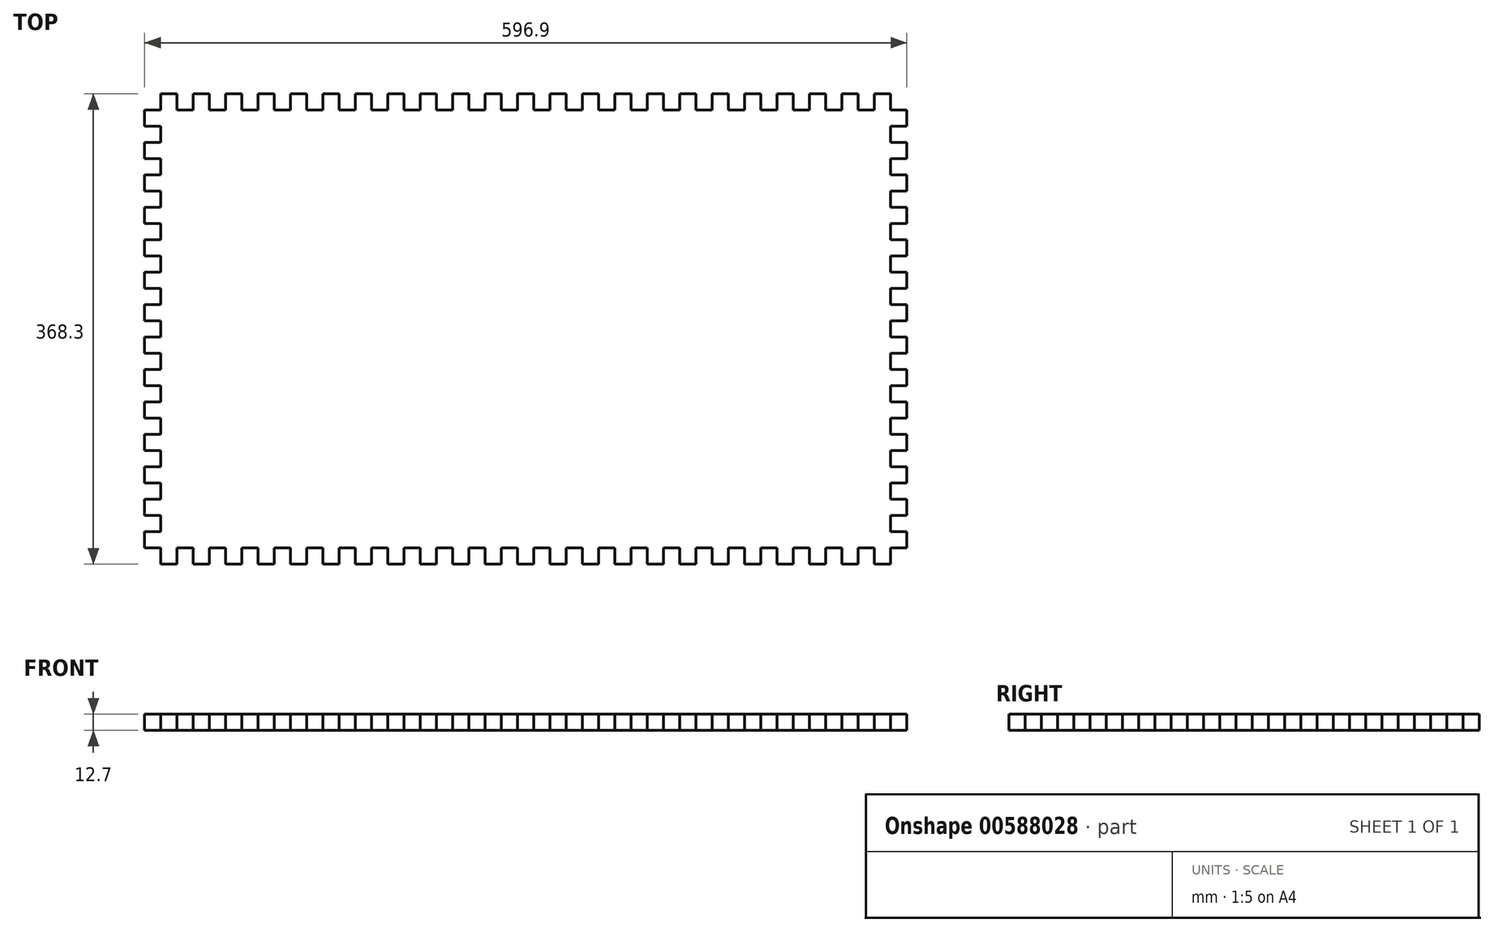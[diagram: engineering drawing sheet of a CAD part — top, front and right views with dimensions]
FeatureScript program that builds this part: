
annotation { "Feature Type Name" : "Feature", "Feature Type Description" : "" }
export const myFeature = defineFeature(function(context is Context, id is Id, definition is map)
    precondition{}
    {
        {
            var Q0;
            Q0=qCreatedBy(makeId("Top.planeOp"),FACE);
            var sketch = newSketch(context, id + "F0", { "sketchPlane" : qUnion([Q0])});
            skLineSegment(sketch, "E0", {"start": v(25.4, 25.4) * mm, "end": v(25.4, 12.7) * mm});
            skLineSegment(sketch, "E1", {"start": v(25.4, 12.7) * mm, "end": v(38.1, 12.7) * mm});
            skLineSegment(sketch, "E2", {"start": v(38.1, 12.7) * mm, "end": v(38.1, 25.4) * mm});
            skLineSegment(sketch, "E3.MirrorCS", {"start": v(50.8, 25.4) * mm, "end": v(50.8, 12.7) * mm});
            skLineSegment(sketch, "E4.MirrorCS", {"start": v(63.5, 12.7) * mm, "end": v(63.5, 25.4) * mm});
            skLineSegment(sketch, "E5.1.0.0", {"start": v(38.1, 25.4) * mm, "end": v(50.8, 25.4) * mm});
            skLineSegment(sketch, "E5.1.0.3", {"start": v(50.8, 12.7) * mm, "end": v(63.5, 12.7) * mm});
            skLineSegment(sketch, "E5.2.0.0", {"start": v(63.5, 25.4) * mm, "end": v(76.2, 25.4) * mm});
            skLineSegment(sketch, "E5.2.0.2", {"start": v(76.2, 25.4) * mm, "end": v(76.2, 12.7) * mm});
            skLineSegment(sketch, "E5.2.0.3", {"start": v(76.2, 12.7) * mm, "end": v(88.9, 12.7) * mm});
            skLineSegment(sketch, "E5.3.0.0", {"start": v(88.9, 25.4) * mm, "end": v(101.6, 25.4) * mm});
            skLineSegment(sketch, "E5.3.0.1", {"start": v(88.9, 12.7) * mm, "end": v(88.9, 25.4) * mm});
            skLineSegment(sketch, "E5.3.0.2", {"start": v(101.6, 25.4) * mm, "end": v(101.6, 12.7) * mm});
            skLineSegment(sketch, "E5.3.0.3", {"start": v(101.6, 12.7) * mm, "end": v(114.3, 12.7) * mm});
            skLineSegment(sketch, "E5.4.0.0", {"start": v(114.3, 25.4) * mm, "end": v(127, 25.4) * mm});
            skLineSegment(sketch, "E5.4.0.1", {"start": v(114.3, 12.7) * mm, "end": v(114.3, 25.4) * mm});
            skLineSegment(sketch, "E5.4.0.2", {"start": v(127, 25.4) * mm, "end": v(127, 12.7) * mm});
            skLineSegment(sketch, "E5.4.0.3", {"start": v(127, 12.7) * mm, "end": v(139.7, 12.7) * mm});
            skLineSegment(sketch, "E5.5.0.0", {"start": v(139.7, 25.4) * mm, "end": v(152.4, 25.4) * mm});
            skLineSegment(sketch, "E5.5.0.1", {"start": v(139.7, 12.7) * mm, "end": v(139.7, 25.4) * mm});
            skLineSegment(sketch, "E5.5.0.2", {"start": v(152.4, 25.4) * mm, "end": v(152.4, 12.7) * mm});
            skLineSegment(sketch, "E5.5.0.3", {"start": v(152.4, 12.7) * mm, "end": v(165.1, 12.7) * mm});
            skLineSegment(sketch, "E5.6.0.0", {"start": v(165.1, 25.4) * mm, "end": v(177.8, 25.4) * mm});
            skLineSegment(sketch, "E5.6.0.1", {"start": v(165.1, 12.7) * mm, "end": v(165.1, 25.4) * mm});
            skLineSegment(sketch, "E5.6.0.2", {"start": v(177.8, 25.4) * mm, "end": v(177.8, 12.7) * mm});
            skLineSegment(sketch, "E5.6.0.3", {"start": v(177.8, 12.7) * mm, "end": v(190.5, 12.7) * mm});
            skLineSegment(sketch, "E5.7.0.0", {"start": v(190.5, 25.4) * mm, "end": v(203.2, 25.4) * mm});
            skLineSegment(sketch, "E5.7.0.1", {"start": v(190.5, 12.7) * mm, "end": v(190.5, 25.4) * mm});
            skLineSegment(sketch, "E5.7.0.2", {"start": v(203.2, 25.4) * mm, "end": v(203.2, 12.7) * mm});
            skLineSegment(sketch, "E5.7.0.3", {"start": v(203.2, 12.7) * mm, "end": v(215.9, 12.7) * mm});
            skLineSegment(sketch, "E5.8.0.0", {"start": v(215.9, 25.4) * mm, "end": v(228.6, 25.4) * mm});
            skLineSegment(sketch, "E5.8.0.1", {"start": v(215.9, 12.7) * mm, "end": v(215.9, 25.4) * mm});
            skLineSegment(sketch, "E5.8.0.2", {"start": v(228.6, 25.4) * mm, "end": v(228.6, 12.7) * mm});
            skLineSegment(sketch, "E5.8.0.3", {"start": v(228.6, 12.7) * mm, "end": v(241.3, 12.7) * mm});
            skLineSegment(sketch, "E5.9.0.0", {"start": v(241.3, 25.4) * mm, "end": v(254, 25.4) * mm});
            skLineSegment(sketch, "E5.9.0.1", {"start": v(241.3, 12.7) * mm, "end": v(241.3, 25.4) * mm});
            skLineSegment(sketch, "E5.9.0.2", {"start": v(254, 25.4) * mm, "end": v(254, 12.7) * mm});
            skLineSegment(sketch, "E5.9.0.3", {"start": v(254, 12.7) * mm, "end": v(266.7, 12.7) * mm});
            skLineSegment(sketch, "E5.10.0.0", {"start": v(266.7, 25.4) * mm, "end": v(279.4, 25.4) * mm});
            skLineSegment(sketch, "E5.10.0.1", {"start": v(266.7, 12.7) * mm, "end": v(266.7, 25.4) * mm});
            skLineSegment(sketch, "E5.10.0.2", {"start": v(279.4, 25.4) * mm, "end": v(279.4, 12.7) * mm});
            skLineSegment(sketch, "E5.10.0.3", {"start": v(279.4, 12.7) * mm, "end": v(292.1, 12.7) * mm});
            skLineSegment(sketch, "E5.11.0.0", {"start": v(292.1, 25.4) * mm, "end": v(304.8, 25.4) * mm});
            skLineSegment(sketch, "E5.11.0.1", {"start": v(292.1, 12.7) * mm, "end": v(292.1, 25.4) * mm});
            skLineSegment(sketch, "E5.11.0.2", {"start": v(304.8, 25.4) * mm, "end": v(304.8, 12.7) * mm});
            skLineSegment(sketch, "E5.11.0.3", {"start": v(304.8, 12.7) * mm, "end": v(317.5, 12.7) * mm});
            skLineSegment(sketch, "E5.12.0.0", {"start": v(317.5, 25.4) * mm, "end": v(330.2, 25.4) * mm});
            skLineSegment(sketch, "E5.12.0.1", {"start": v(317.5, 12.7) * mm, "end": v(317.5, 25.4) * mm});
            skLineSegment(sketch, "E5.12.0.2", {"start": v(330.2, 25.4) * mm, "end": v(330.2, 12.7) * mm});
            skLineSegment(sketch, "E5.12.0.3", {"start": v(330.2, 12.7) * mm, "end": v(342.9, 12.7) * mm});
            skLineSegment(sketch, "E5.13.0.0", {"start": v(342.9, 25.4) * mm, "end": v(355.6, 25.4) * mm});
            skLineSegment(sketch, "E5.13.0.1", {"start": v(342.9, 12.7) * mm, "end": v(342.9, 25.4) * mm});
            skLineSegment(sketch, "E5.13.0.2", {"start": v(355.6, 25.4) * mm, "end": v(355.6, 12.7) * mm});
            skLineSegment(sketch, "E5.13.0.3", {"start": v(355.6, 12.7) * mm, "end": v(368.3, 12.7) * mm});
            skLineSegment(sketch, "E5.14.0.0", {"start": v(368.3, 25.4) * mm, "end": v(381, 25.4) * mm});
            skLineSegment(sketch, "E5.14.0.1", {"start": v(368.3, 12.7) * mm, "end": v(368.3, 25.4) * mm});
            skLineSegment(sketch, "E5.14.0.2", {"start": v(381, 25.4) * mm, "end": v(381, 12.7) * mm});
            skLineSegment(sketch, "E5.14.0.3", {"start": v(381, 12.7) * mm, "end": v(393.7, 12.7) * mm});
            skLineSegment(sketch, "E5.15.0.0", {"start": v(393.7, 25.4) * mm, "end": v(406.4, 25.4) * mm});
            skLineSegment(sketch, "E5.15.0.1", {"start": v(393.7, 12.7) * mm, "end": v(393.7, 25.4) * mm});
            skLineSegment(sketch, "E5.15.0.2", {"start": v(406.4, 25.4) * mm, "end": v(406.4, 12.7) * mm});
            skLineSegment(sketch, "E5.15.0.3", {"start": v(406.4, 12.7) * mm, "end": v(419.1, 12.7) * mm});
            skLineSegment(sketch, "E5.16.0.0", {"start": v(419.1, 25.4) * mm, "end": v(431.8, 25.4) * mm});
            skLineSegment(sketch, "E5.16.0.1", {"start": v(419.1, 12.7) * mm, "end": v(419.1, 25.4) * mm});
            skLineSegment(sketch, "E5.16.0.2", {"start": v(431.8, 25.4) * mm, "end": v(431.8, 12.7) * mm});
            skLineSegment(sketch, "E5.16.0.3", {"start": v(431.8, 12.7) * mm, "end": v(444.5, 12.7) * mm});
            skLineSegment(sketch, "E5.17.0.0", {"start": v(444.5, 25.4) * mm, "end": v(457.2, 25.4) * mm});
            skLineSegment(sketch, "E5.17.0.1", {"start": v(444.5, 12.7) * mm, "end": v(444.5, 25.4) * mm});
            skLineSegment(sketch, "E5.17.0.2", {"start": v(457.2, 25.4) * mm, "end": v(457.2, 12.7) * mm});
            skLineSegment(sketch, "E5.17.0.3", {"start": v(457.2, 12.7) * mm, "end": v(469.9, 12.7) * mm});
            skLineSegment(sketch, "E5.18.0.0", {"start": v(469.9, 25.4) * mm, "end": v(482.6, 25.4) * mm});
            skLineSegment(sketch, "E5.18.0.1", {"start": v(469.9, 12.7) * mm, "end": v(469.9, 25.4) * mm});
            skLineSegment(sketch, "E5.18.0.2", {"start": v(482.6, 25.4) * mm, "end": v(482.6, 12.7) * mm});
            skLineSegment(sketch, "E5.18.0.3", {"start": v(482.6, 12.7) * mm, "end": v(495.3, 12.7) * mm});
            skLineSegment(sketch, "E5.19.0.0", {"start": v(495.3, 25.4) * mm, "end": v(508, 25.4) * mm});
            skLineSegment(sketch, "E5.19.0.1", {"start": v(495.3, 12.7) * mm, "end": v(495.3, 25.4) * mm});
            skLineSegment(sketch, "E5.19.0.2", {"start": v(508, 25.4) * mm, "end": v(508, 12.7) * mm});
            skLineSegment(sketch, "E5.19.0.3", {"start": v(508, 12.7) * mm, "end": v(520.7, 12.7) * mm});
            skLineSegment(sketch, "E5.20.0.0", {"start": v(520.7, 25.4) * mm, "end": v(533.4, 25.4) * mm});
            skLineSegment(sketch, "E5.20.0.1", {"start": v(520.7, 12.7) * mm, "end": v(520.7, 25.4) * mm});
            skLineSegment(sketch, "E5.20.0.2", {"start": v(533.4, 25.4) * mm, "end": v(533.4, 12.7) * mm});
            skLineSegment(sketch, "E5.20.0.3", {"start": v(533.4, 12.7) * mm, "end": v(546.1, 12.7) * mm});
            skLineSegment(sketch, "E5.21.0.0", {"start": v(546.1, 25.4) * mm, "end": v(558.8, 25.4) * mm});
            skLineSegment(sketch, "E5.21.0.1", {"start": v(546.1, 12.7) * mm, "end": v(546.1, 25.4) * mm});
            skLineSegment(sketch, "E5.21.0.2", {"start": v(558.8, 25.4) * mm, "end": v(558.8, 12.7) * mm});
            skLineSegment(sketch, "E5.21.0.3", {"start": v(558.8, 12.7) * mm, "end": v(571.5, 12.7) * mm});
            skLineSegment(sketch, "E5.22.0.0", {"start": v(571.5, 25.4) * mm, "end": v(584.2, 25.4) * mm});
            skLineSegment(sketch, "E5.22.0.1", {"start": v(571.5, 12.7) * mm, "end": v(571.5, 25.4) * mm});
            skLineSegment(sketch, "E5.22.0.2", {"start": v(584.2, 25.4) * mm, "end": v(584.2, 12.7) * mm});
            skLineSegment(sketch, "E5.23.0.1", {"start": v(584.2, 12.7) * mm, "end": v(584.2, 25.4) * mm});
            skLineSegment(sketch, "E6", {"start": v(609.6, 368.3) * mm, "end": v(596.9, 368.3) * mm});
            skLineSegment(sketch, "E7", {"start": v(596.9, 368.3) * mm, "end": v(596.9, 381) * mm});
            skLineSegment(sketch, "E8", {"start": v(596.9, 381) * mm, "end": v(584.2, 381) * mm});
            skLineSegment(sketch, "E9", {"start": v(584.2, 381) * mm, "end": v(584.2, 368.3) * mm});
            skLineSegment(sketch, "E10.1.0.0", {"start": v(584.2, 368.3) * mm, "end": v(571.5, 368.3) * mm});
            skLineSegment(sketch, "E10.1.0.1", {"start": v(571.5, 368.3) * mm, "end": v(571.5, 381) * mm});
            skLineSegment(sketch, "E10.1.0.2", {"start": v(571.5, 381) * mm, "end": v(558.8, 381) * mm});
            skLineSegment(sketch, "E10.1.0.3", {"start": v(558.8, 381) * mm, "end": v(558.8, 368.3) * mm});
            skLineSegment(sketch, "E10.2.0.0", {"start": v(558.8, 368.3) * mm, "end": v(546.1, 368.3) * mm});
            skLineSegment(sketch, "E10.2.0.1", {"start": v(546.1, 368.3) * mm, "end": v(546.1, 381) * mm});
            skLineSegment(sketch, "E10.2.0.2", {"start": v(546.1, 381) * mm, "end": v(533.4, 381) * mm});
            skLineSegment(sketch, "E10.2.0.3", {"start": v(533.4, 381) * mm, "end": v(533.4, 368.3) * mm});
            skLineSegment(sketch, "E10.3.0.0", {"start": v(533.4, 368.3) * mm, "end": v(520.7, 368.3) * mm});
            skLineSegment(sketch, "E10.3.0.1", {"start": v(520.7, 368.3) * mm, "end": v(520.7, 381) * mm});
            skLineSegment(sketch, "E10.3.0.2", {"start": v(520.7, 381) * mm, "end": v(508, 381) * mm});
            skLineSegment(sketch, "E10.3.0.3", {"start": v(508, 381) * mm, "end": v(508, 368.3) * mm});
            skLineSegment(sketch, "E10.4.0.0", {"start": v(508, 368.3) * mm, "end": v(495.3, 368.3) * mm});
            skLineSegment(sketch, "E10.4.0.1", {"start": v(495.3, 368.3) * mm, "end": v(495.3, 381) * mm});
            skLineSegment(sketch, "E10.4.0.2", {"start": v(495.3, 381) * mm, "end": v(482.6, 381) * mm});
            skLineSegment(sketch, "E10.4.0.3", {"start": v(482.6, 381) * mm, "end": v(482.6, 368.3) * mm});
            skLineSegment(sketch, "E10.5.0.0", {"start": v(482.6, 368.3) * mm, "end": v(469.9, 368.3) * mm});
            skLineSegment(sketch, "E10.5.0.1", {"start": v(469.9, 368.3) * mm, "end": v(469.9, 381) * mm});
            skLineSegment(sketch, "E10.5.0.2", {"start": v(469.9, 381) * mm, "end": v(457.2, 381) * mm});
            skLineSegment(sketch, "E10.5.0.3", {"start": v(457.2, 381) * mm, "end": v(457.2, 368.3) * mm});
            skLineSegment(sketch, "E10.6.0.0", {"start": v(457.2, 368.3) * mm, "end": v(444.5, 368.3) * mm});
            skLineSegment(sketch, "E10.6.0.1", {"start": v(444.5, 368.3) * mm, "end": v(444.5, 381) * mm});
            skLineSegment(sketch, "E10.6.0.2", {"start": v(444.5, 381) * mm, "end": v(431.8, 381) * mm});
            skLineSegment(sketch, "E10.6.0.3", {"start": v(431.8, 381) * mm, "end": v(431.8, 368.3) * mm});
            skLineSegment(sketch, "E10.7.0.0", {"start": v(431.8, 368.3) * mm, "end": v(419.1, 368.3) * mm});
            skLineSegment(sketch, "E10.7.0.1", {"start": v(419.1, 368.3) * mm, "end": v(419.1, 381) * mm});
            skLineSegment(sketch, "E10.7.0.2", {"start": v(419.1, 381) * mm, "end": v(406.4, 381) * mm});
            skLineSegment(sketch, "E10.7.0.3", {"start": v(406.4, 381) * mm, "end": v(406.4, 368.3) * mm});
            skLineSegment(sketch, "E10.8.0.0", {"start": v(406.4, 368.3) * mm, "end": v(393.7, 368.3) * mm});
            skLineSegment(sketch, "E10.8.0.1", {"start": v(393.7, 368.3) * mm, "end": v(393.7, 381) * mm});
            skLineSegment(sketch, "E10.8.0.2", {"start": v(393.7, 381) * mm, "end": v(381, 381) * mm});
            skLineSegment(sketch, "E10.8.0.3", {"start": v(381, 381) * mm, "end": v(381, 368.3) * mm});
            skLineSegment(sketch, "E10.9.0.0", {"start": v(381, 368.3) * mm, "end": v(368.3, 368.3) * mm});
            skLineSegment(sketch, "E10.9.0.1", {"start": v(368.3, 368.3) * mm, "end": v(368.3, 381) * mm});
            skLineSegment(sketch, "E10.9.0.2", {"start": v(368.3, 381) * mm, "end": v(355.6, 381) * mm});
            skLineSegment(sketch, "E10.9.0.3", {"start": v(355.6, 381) * mm, "end": v(355.6, 368.3) * mm});
            skLineSegment(sketch, "E10.10.0.0", {"start": v(355.6, 368.3) * mm, "end": v(342.9, 368.3) * mm});
            skLineSegment(sketch, "E10.10.0.1", {"start": v(342.9, 368.3) * mm, "end": v(342.9, 381) * mm});
            skLineSegment(sketch, "E10.10.0.2", {"start": v(342.9, 381) * mm, "end": v(330.2, 381) * mm});
            skLineSegment(sketch, "E10.10.0.3", {"start": v(330.2, 381) * mm, "end": v(330.2, 368.3) * mm});
            skLineSegment(sketch, "E10.11.0.0", {"start": v(330.2, 368.3) * mm, "end": v(317.5, 368.3) * mm});
            skLineSegment(sketch, "E10.11.0.1", {"start": v(317.5, 368.3) * mm, "end": v(317.5, 381) * mm});
            skLineSegment(sketch, "E10.11.0.2", {"start": v(317.5, 381) * mm, "end": v(304.8, 381) * mm});
            skLineSegment(sketch, "E10.11.0.3", {"start": v(304.8, 381) * mm, "end": v(304.8, 368.3) * mm});
            skLineSegment(sketch, "E10.12.0.0", {"start": v(304.8, 368.3) * mm, "end": v(292.1, 368.3) * mm});
            skLineSegment(sketch, "E10.12.0.1", {"start": v(292.1, 368.3) * mm, "end": v(292.1, 381) * mm});
            skLineSegment(sketch, "E10.12.0.2", {"start": v(292.1, 381) * mm, "end": v(279.4, 381) * mm});
            skLineSegment(sketch, "E10.12.0.3", {"start": v(279.4, 381) * mm, "end": v(279.4, 368.3) * mm});
            skLineSegment(sketch, "E10.13.0.0", {"start": v(279.4, 368.3) * mm, "end": v(266.7, 368.3) * mm});
            skLineSegment(sketch, "E10.13.0.1", {"start": v(266.7, 368.3) * mm, "end": v(266.7, 381) * mm});
            skLineSegment(sketch, "E10.13.0.2", {"start": v(266.7, 381) * mm, "end": v(254, 381) * mm});
            skLineSegment(sketch, "E10.13.0.3", {"start": v(254, 381) * mm, "end": v(254, 368.3) * mm});
            skLineSegment(sketch, "E10.14.0.0", {"start": v(254, 368.3) * mm, "end": v(241.3, 368.3) * mm});
            skLineSegment(sketch, "E10.14.0.1", {"start": v(241.3, 368.3) * mm, "end": v(241.3, 381) * mm});
            skLineSegment(sketch, "E10.14.0.2", {"start": v(241.3, 381) * mm, "end": v(228.6, 381) * mm});
            skLineSegment(sketch, "E10.14.0.3", {"start": v(228.6, 381) * mm, "end": v(228.6, 368.3) * mm});
            skLineSegment(sketch, "E10.15.0.0", {"start": v(228.6, 368.3) * mm, "end": v(215.9, 368.3) * mm});
            skLineSegment(sketch, "E10.15.0.1", {"start": v(215.9, 368.3) * mm, "end": v(215.9, 381) * mm});
            skLineSegment(sketch, "E10.15.0.2", {"start": v(215.9, 381) * mm, "end": v(203.2, 381) * mm});
            skLineSegment(sketch, "E10.15.0.3", {"start": v(203.2, 381) * mm, "end": v(203.2, 368.3) * mm});
            skLineSegment(sketch, "E10.16.0.0", {"start": v(203.2, 368.3) * mm, "end": v(190.5, 368.3) * mm});
            skLineSegment(sketch, "E10.16.0.1", {"start": v(190.5, 368.3) * mm, "end": v(190.5, 381) * mm});
            skLineSegment(sketch, "E10.16.0.2", {"start": v(190.5, 381) * mm, "end": v(177.8, 381) * mm});
            skLineSegment(sketch, "E10.16.0.3", {"start": v(177.8, 381) * mm, "end": v(177.8, 368.3) * mm});
            skLineSegment(sketch, "E10.17.0.0", {"start": v(177.8, 368.3) * mm, "end": v(165.1, 368.3) * mm});
            skLineSegment(sketch, "E10.17.0.1", {"start": v(165.1, 368.3) * mm, "end": v(165.1, 381) * mm});
            skLineSegment(sketch, "E10.17.0.2", {"start": v(165.1, 381) * mm, "end": v(152.4, 381) * mm});
            skLineSegment(sketch, "E10.17.0.3", {"start": v(152.4, 381) * mm, "end": v(152.4, 368.3) * mm});
            skLineSegment(sketch, "E10.18.0.0", {"start": v(152.4, 368.3) * mm, "end": v(139.7, 368.3) * mm});
            skLineSegment(sketch, "E10.18.0.1", {"start": v(139.7, 368.3) * mm, "end": v(139.7, 381) * mm});
            skLineSegment(sketch, "E10.18.0.2", {"start": v(139.7, 381) * mm, "end": v(127, 381) * mm});
            skLineSegment(sketch, "E10.18.0.3", {"start": v(127, 381) * mm, "end": v(127, 368.3) * mm});
            skLineSegment(sketch, "E10.19.0.0", {"start": v(127, 368.3) * mm, "end": v(114.3, 368.3) * mm});
            skLineSegment(sketch, "E10.19.0.1", {"start": v(114.3, 368.3) * mm, "end": v(114.3, 381) * mm});
            skLineSegment(sketch, "E10.19.0.2", {"start": v(114.3, 381) * mm, "end": v(101.6, 381) * mm});
            skLineSegment(sketch, "E10.19.0.3", {"start": v(101.6, 381) * mm, "end": v(101.6, 368.3) * mm});
            skLineSegment(sketch, "E10.20.0.0", {"start": v(101.6, 368.3) * mm, "end": v(88.9, 368.3) * mm});
            skLineSegment(sketch, "E10.20.0.1", {"start": v(88.9, 368.3) * mm, "end": v(88.9, 381) * mm});
            skLineSegment(sketch, "E10.20.0.2", {"start": v(88.9, 381) * mm, "end": v(76.2, 381) * mm});
            skLineSegment(sketch, "E10.20.0.3", {"start": v(76.2, 381) * mm, "end": v(76.2, 368.3) * mm});
            skLineSegment(sketch, "E10.21.0.0", {"start": v(76.2, 368.3) * mm, "end": v(63.5, 368.3) * mm});
            skLineSegment(sketch, "E10.21.0.1", {"start": v(63.5, 368.3) * mm, "end": v(63.5, 381) * mm});
            skLineSegment(sketch, "E10.21.0.2", {"start": v(63.5, 381) * mm, "end": v(50.8, 381) * mm});
            skLineSegment(sketch, "E10.21.0.3", {"start": v(50.8, 381) * mm, "end": v(50.8, 368.3) * mm});
            skLineSegment(sketch, "E10.22.0.0", {"start": v(50.8, 368.3) * mm, "end": v(38.1, 368.3) * mm});
            skLineSegment(sketch, "E10.22.0.1", {"start": v(38.1, 368.3) * mm, "end": v(38.1, 381) * mm});
            skLineSegment(sketch, "E10.22.0.2", {"start": v(38.1, 381) * mm, "end": v(25.4, 381) * mm});
            skLineSegment(sketch, "E10.22.0.3", {"start": v(25.4, 381) * mm, "end": v(25.4, 368.3) * mm});
            skLineSegment(sketch, "E11", {"start": v(12.7, 38.1) * mm, "end": v(25.4, 38.1) * mm});
            skLineSegment(sketch, "E12", {"start": v(25.4, 38.1) * mm, "end": v(25.4, 50.8) * mm});
            skLineSegment(sketch, "E13", {"start": v(25.4, 50.8) * mm, "end": v(12.7, 50.8) * mm});
            skLineSegment(sketch, "E14.0.1.0", {"start": v(12.7, 50.8) * mm, "end": v(12.7, 63.5) * mm});
            skLineSegment(sketch, "E14.0.1.1", {"start": v(12.7, 63.5) * mm, "end": v(25.4, 63.5) * mm});
            skLineSegment(sketch, "E14.0.1.2", {"start": v(25.4, 63.5) * mm, "end": v(25.4, 76.2) * mm});
            skLineSegment(sketch, "E14.0.1.3", {"start": v(25.4, 76.2) * mm, "end": v(12.7, 76.2) * mm});
            skLineSegment(sketch, "E14.0.2.0", {"start": v(12.7, 76.2) * mm, "end": v(12.7, 88.9) * mm});
            skLineSegment(sketch, "E14.0.2.1", {"start": v(12.7, 88.9) * mm, "end": v(25.4, 88.9) * mm});
            skLineSegment(sketch, "E14.0.2.2", {"start": v(25.4, 88.9) * mm, "end": v(25.4, 101.6) * mm});
            skLineSegment(sketch, "E14.0.2.3", {"start": v(25.4, 101.6) * mm, "end": v(12.7, 101.6) * mm});
            skLineSegment(sketch, "E14.0.3.0", {"start": v(12.7, 101.6) * mm, "end": v(12.7, 114.3) * mm});
            skLineSegment(sketch, "E14.0.3.1", {"start": v(12.7, 114.3) * mm, "end": v(25.4, 114.3) * mm});
            skLineSegment(sketch, "E14.0.3.2", {"start": v(25.4, 114.3) * mm, "end": v(25.4, 127) * mm});
            skLineSegment(sketch, "E14.0.3.3", {"start": v(25.4, 127) * mm, "end": v(12.7, 127) * mm});
            skLineSegment(sketch, "E14.0.4.0", {"start": v(12.7, 127) * mm, "end": v(12.7, 139.7) * mm});
            skLineSegment(sketch, "E14.0.4.1", {"start": v(12.7, 139.7) * mm, "end": v(25.4, 139.7) * mm});
            skLineSegment(sketch, "E14.0.4.2", {"start": v(25.4, 139.7) * mm, "end": v(25.4, 152.4) * mm});
            skLineSegment(sketch, "E14.0.4.3", {"start": v(25.4, 152.4) * mm, "end": v(12.7, 152.4) * mm});
            skLineSegment(sketch, "E14.0.5.0", {"start": v(12.7, 152.4) * mm, "end": v(12.7, 165.1) * mm});
            skLineSegment(sketch, "E14.0.5.1", {"start": v(12.7, 165.1) * mm, "end": v(25.4, 165.1) * mm});
            skLineSegment(sketch, "E14.0.5.2", {"start": v(25.4, 165.1) * mm, "end": v(25.4, 177.8) * mm});
            skLineSegment(sketch, "E14.0.5.3", {"start": v(25.4, 177.8) * mm, "end": v(12.7, 177.8) * mm});
            skLineSegment(sketch, "E14.0.6.0", {"start": v(12.7, 177.8) * mm, "end": v(12.7, 190.5) * mm});
            skLineSegment(sketch, "E14.0.6.1", {"start": v(12.7, 190.5) * mm, "end": v(25.4, 190.5) * mm});
            skLineSegment(sketch, "E14.0.6.2", {"start": v(25.4, 190.5) * mm, "end": v(25.4, 203.2) * mm});
            skLineSegment(sketch, "E14.0.6.3", {"start": v(25.4, 203.2) * mm, "end": v(12.7, 203.2) * mm});
            skLineSegment(sketch, "E14.0.7.0", {"start": v(12.7, 203.2) * mm, "end": v(12.7, 215.9) * mm});
            skLineSegment(sketch, "E14.0.7.1", {"start": v(12.7, 215.9) * mm, "end": v(25.4, 215.9) * mm});
            skLineSegment(sketch, "E14.0.7.2", {"start": v(25.4, 215.9) * mm, "end": v(25.4, 228.6) * mm});
            skLineSegment(sketch, "E14.0.7.3", {"start": v(25.4, 228.6) * mm, "end": v(12.7, 228.6) * mm});
            skLineSegment(sketch, "E14.0.8.0", {"start": v(12.7, 228.6) * mm, "end": v(12.7, 241.3) * mm});
            skLineSegment(sketch, "E14.0.8.1", {"start": v(12.7, 241.3) * mm, "end": v(25.4, 241.3) * mm});
            skLineSegment(sketch, "E14.0.8.2", {"start": v(25.4, 241.3) * mm, "end": v(25.4, 254) * mm});
            skLineSegment(sketch, "E14.0.8.3", {"start": v(25.4, 254) * mm, "end": v(12.7, 254) * mm});
            skLineSegment(sketch, "E14.0.9.0", {"start": v(12.7, 254) * mm, "end": v(12.7, 266.7) * mm});
            skLineSegment(sketch, "E14.0.9.1", {"start": v(12.7, 266.7) * mm, "end": v(25.4, 266.7) * mm});
            skLineSegment(sketch, "E14.0.9.2", {"start": v(25.4, 266.7) * mm, "end": v(25.4, 279.4) * mm});
            skLineSegment(sketch, "E14.0.9.3", {"start": v(25.4, 279.4) * mm, "end": v(12.7, 279.4) * mm});
            skLineSegment(sketch, "E14.0.10.0", {"start": v(12.7, 279.4) * mm, "end": v(12.7, 292.1) * mm});
            skLineSegment(sketch, "E14.0.10.1", {"start": v(12.7, 292.1) * mm, "end": v(25.4, 292.1) * mm});
            skLineSegment(sketch, "E14.0.10.2", {"start": v(25.4, 292.1) * mm, "end": v(25.4, 304.8) * mm});
            skLineSegment(sketch, "E14.0.10.3", {"start": v(25.4, 304.8) * mm, "end": v(12.7, 304.8) * mm});
            skLineSegment(sketch, "E14.0.11.0", {"start": v(12.7, 304.8) * mm, "end": v(12.7, 317.5) * mm});
            skLineSegment(sketch, "E14.0.11.1", {"start": v(12.7, 317.5) * mm, "end": v(25.4, 317.5) * mm});
            skLineSegment(sketch, "E14.0.11.2", {"start": v(25.4, 317.5) * mm, "end": v(25.4, 330.2) * mm});
            skLineSegment(sketch, "E14.0.11.3", {"start": v(25.4, 330.2) * mm, "end": v(12.7, 330.2) * mm});
            skLineSegment(sketch, "E14.0.12.0", {"start": v(12.7, 330.2) * mm, "end": v(12.7, 342.9) * mm});
            skLineSegment(sketch, "E14.0.12.1", {"start": v(12.7, 342.9) * mm, "end": v(25.4, 342.9) * mm});
            skLineSegment(sketch, "E14.0.12.2", {"start": v(25.4, 342.9) * mm, "end": v(25.4, 355.6) * mm});
            skLineSegment(sketch, "E14.0.12.3", {"start": v(25.4, 355.6) * mm, "end": v(12.7, 355.6) * mm});
            skLineSegment(sketch, "E14.0.13.0", {"start": v(12.7, 355.6) * mm, "end": v(12.7, 368.3) * mm});
            skLineSegment(sketch, "E14.0.13.1", {"start": v(12.7, 368.3) * mm, "end": v(25.4, 368.3) * mm});
            skLineSegment(sketch, "E15", {"start": v(609.6, 368.3) * mm, "end": v(609.6, 355.6) * mm});
            skLineSegment(sketch, "E16", {"start": v(609.6, 355.6) * mm, "end": v(596.9, 355.6) * mm});
            skLineSegment(sketch, "E17", {"start": v(596.9, 355.6) * mm, "end": v(596.9, 342.9) * mm});
            skLineSegment(sketch, "E18.0.1.0", {"start": v(609.6, 342.9) * mm, "end": v(596.9, 342.9) * mm});
            skLineSegment(sketch, "E18.0.1.1", {"start": v(609.6, 342.9) * mm, "end": v(609.6, 330.2) * mm});
            skLineSegment(sketch, "E18.0.1.2", {"start": v(609.6, 330.2) * mm, "end": v(596.9, 330.2) * mm});
            skLineSegment(sketch, "E18.0.1.3", {"start": v(596.9, 330.2) * mm, "end": v(596.9, 317.5) * mm});
            skLineSegment(sketch, "E18.0.2.0", {"start": v(609.6, 317.5) * mm, "end": v(596.9, 317.5) * mm});
            skLineSegment(sketch, "E18.0.2.1", {"start": v(609.6, 317.5) * mm, "end": v(609.6, 304.8) * mm});
            skLineSegment(sketch, "E18.0.2.2", {"start": v(609.6, 304.8) * mm, "end": v(596.9, 304.8) * mm});
            skLineSegment(sketch, "E18.0.2.3", {"start": v(596.9, 304.8) * mm, "end": v(596.9, 292.1) * mm});
            skLineSegment(sketch, "E18.0.3.0", {"start": v(609.6, 292.1) * mm, "end": v(596.9, 292.1) * mm});
            skLineSegment(sketch, "E18.0.3.1", {"start": v(609.6, 292.1) * mm, "end": v(609.6, 279.4) * mm});
            skLineSegment(sketch, "E18.0.3.2", {"start": v(609.6, 279.4) * mm, "end": v(596.9, 279.4) * mm});
            skLineSegment(sketch, "E18.0.3.3", {"start": v(596.9, 279.4) * mm, "end": v(596.9, 266.7) * mm});
            skLineSegment(sketch, "E18.0.4.0", {"start": v(609.6, 266.7) * mm, "end": v(596.9, 266.7) * mm});
            skLineSegment(sketch, "E18.0.4.1", {"start": v(609.6, 266.7) * mm, "end": v(609.6, 254) * mm});
            skLineSegment(sketch, "E18.0.4.2", {"start": v(609.6, 254) * mm, "end": v(596.9, 254) * mm});
            skLineSegment(sketch, "E18.0.4.3", {"start": v(596.9, 254) * mm, "end": v(596.9, 241.3) * mm});
            skLineSegment(sketch, "E18.0.5.0", {"start": v(609.6, 241.3) * mm, "end": v(596.9, 241.3) * mm});
            skLineSegment(sketch, "E18.0.5.1", {"start": v(609.6, 241.3) * mm, "end": v(609.6, 228.6) * mm});
            skLineSegment(sketch, "E18.0.5.2", {"start": v(609.6, 228.6) * mm, "end": v(596.9, 228.6) * mm});
            skLineSegment(sketch, "E18.0.5.3", {"start": v(596.9, 228.6) * mm, "end": v(596.9, 215.9) * mm});
            skLineSegment(sketch, "E18.0.6.0", {"start": v(609.6, 215.9) * mm, "end": v(596.9, 215.9) * mm});
            skLineSegment(sketch, "E18.0.6.1", {"start": v(609.6, 215.9) * mm, "end": v(609.6, 203.2) * mm});
            skLineSegment(sketch, "E18.0.6.2", {"start": v(609.6, 203.2) * mm, "end": v(596.9, 203.2) * mm});
            skLineSegment(sketch, "E18.0.6.3", {"start": v(596.9, 203.2) * mm, "end": v(596.9, 190.5) * mm});
            skLineSegment(sketch, "E18.0.7.0", {"start": v(609.6, 190.5) * mm, "end": v(596.9, 190.5) * mm});
            skLineSegment(sketch, "E18.0.7.1", {"start": v(609.6, 190.5) * mm, "end": v(609.6, 177.8) * mm});
            skLineSegment(sketch, "E18.0.7.2", {"start": v(609.6, 177.8) * mm, "end": v(596.9, 177.8) * mm});
            skLineSegment(sketch, "E18.0.7.3", {"start": v(596.9, 177.8) * mm, "end": v(596.9, 165.1) * mm});
            skLineSegment(sketch, "E18.0.8.0", {"start": v(609.6, 165.1) * mm, "end": v(596.9, 165.1) * mm});
            skLineSegment(sketch, "E18.0.8.1", {"start": v(609.6, 165.1) * mm, "end": v(609.6, 152.4) * mm});
            skLineSegment(sketch, "E18.0.8.2", {"start": v(609.6, 152.4) * mm, "end": v(596.9, 152.4) * mm});
            skLineSegment(sketch, "E18.0.8.3", {"start": v(596.9, 152.4) * mm, "end": v(596.9, 139.7) * mm});
            skLineSegment(sketch, "E18.0.9.0", {"start": v(609.6, 139.7) * mm, "end": v(596.9, 139.7) * mm});
            skLineSegment(sketch, "E18.0.9.1", {"start": v(609.6, 139.7) * mm, "end": v(609.6, 127) * mm});
            skLineSegment(sketch, "E18.0.9.2", {"start": v(609.6, 127) * mm, "end": v(596.9, 127) * mm});
            skLineSegment(sketch, "E18.0.9.3", {"start": v(596.9, 127) * mm, "end": v(596.9, 114.3) * mm});
            skLineSegment(sketch, "E18.0.10.0", {"start": v(609.6, 114.3) * mm, "end": v(596.9, 114.3) * mm});
            skLineSegment(sketch, "E18.0.10.1", {"start": v(609.6, 114.3) * mm, "end": v(609.6, 101.6) * mm});
            skLineSegment(sketch, "E18.0.10.2", {"start": v(609.6, 101.6) * mm, "end": v(596.9, 101.6) * mm});
            skLineSegment(sketch, "E18.0.10.3", {"start": v(596.9, 101.6) * mm, "end": v(596.9, 88.9) * mm});
            skLineSegment(sketch, "E18.0.11.0", {"start": v(609.6, 88.9) * mm, "end": v(596.9, 88.9) * mm});
            skLineSegment(sketch, "E18.0.11.1", {"start": v(609.6, 88.9) * mm, "end": v(609.6, 76.2) * mm});
            skLineSegment(sketch, "E18.0.11.2", {"start": v(609.6, 76.2) * mm, "end": v(596.9, 76.2) * mm});
            skLineSegment(sketch, "E18.0.11.3", {"start": v(596.9, 76.2) * mm, "end": v(596.9, 63.5) * mm});
            skLineSegment(sketch, "E18.0.12.0", {"start": v(609.6, 63.5) * mm, "end": v(596.9, 63.5) * mm});
            skLineSegment(sketch, "E18.0.12.1", {"start": v(609.6, 63.5) * mm, "end": v(609.6, 50.8) * mm});
            skLineSegment(sketch, "E18.0.12.2", {"start": v(609.6, 50.8) * mm, "end": v(596.9, 50.8) * mm});
            skLineSegment(sketch, "E18.0.12.3", {"start": v(596.9, 50.8) * mm, "end": v(596.9, 38.1) * mm});
            skLineSegment(sketch, "E18.0.13.0", {"start": v(609.6, 38.1) * mm, "end": v(596.9, 38.1) * mm});
            skLineSegment(sketch, "E18.0.13.1", {"start": v(609.6, 38.1) * mm, "end": v(609.6, 25.4) * mm});
            skLineSegment(sketch, "E18.0.13.2", {"start": v(609.6, 25.4) * mm, "end": v(596.9, 25.4) * mm});
            skLineSegment(sketch, "E19", {"start": v(12.7, 38.1) * mm, "end": v(12.7, 25.4) * mm});
            skLineSegment(sketch, "E20", {"start": v(12.7, 25.4) * mm, "end": v(25.4, 25.4) * mm});
            skLineSegment(sketch, "E21", {"start": v(584.2, 12.7) * mm, "end": v(596.9, 12.7) * mm});
            skLineSegment(sketch, "E22", {"start": v(596.9, 12.7) * mm, "end": v(596.9, 25.4) * mm});
            skSolve(sketch);
        }
        {
            var Q0;
            Q0 = qSketchRegion(id + "F0", true);
            extrude(context, id + "F1", {"entities" : qUnion([Q0]), "depth" : 12.7 * mm, "offsetDistance" : 25.4 * mm});
        }
    });
